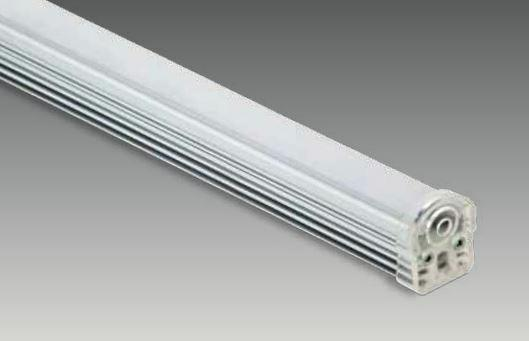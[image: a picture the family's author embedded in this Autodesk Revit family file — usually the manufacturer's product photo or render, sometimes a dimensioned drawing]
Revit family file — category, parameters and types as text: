
# Revit family: SD 0135 CVK-II
name_source: partatom
category: Lighting Fixtures
revit_build: Autodesk Revit 2017 (Build: 20160225_1515(x64)
units: mm (PartAtom-declared; Revit-internal decimal feet)

## family parameters
Cut with Voids When Loaded = No
Host = Face
Light Source = Yes
Part Type = Normal
Room Calculation Point = No
Round Connector Dimension = Use Diameter
Shared = No

## types (2) — shared parameters
Apparent Load = 3 VA
Color Filter = 16777215
Default Elevation = 1219 mm
Dimming Lamp Color Temperature Shift = <None>
Emit Shape Visible in Rendering = Yes
Emit from Rectangle Length = 15 mm  [stored 0.0492126 ft]
Emit from Rectangle Width = 130 mm  [stored 0.426509 ft]
Light Source Symbol Size = 610 mm
Manufacturer = ARLIGHT
Type Image = SD 0135 CVK.JPG
Wattage Comments = 3

## type names (no varying parameters)
- SDCVK.135.3.30
- SDCVK.135.3.40

note: [stored X ft] marks values corroborated as IEEE doubles in the binary element streams (Revit-internal decimal feet)

## geometry (parser evidence)
native form markers: Sweep x3
no freeform markers — native parametric forms only
